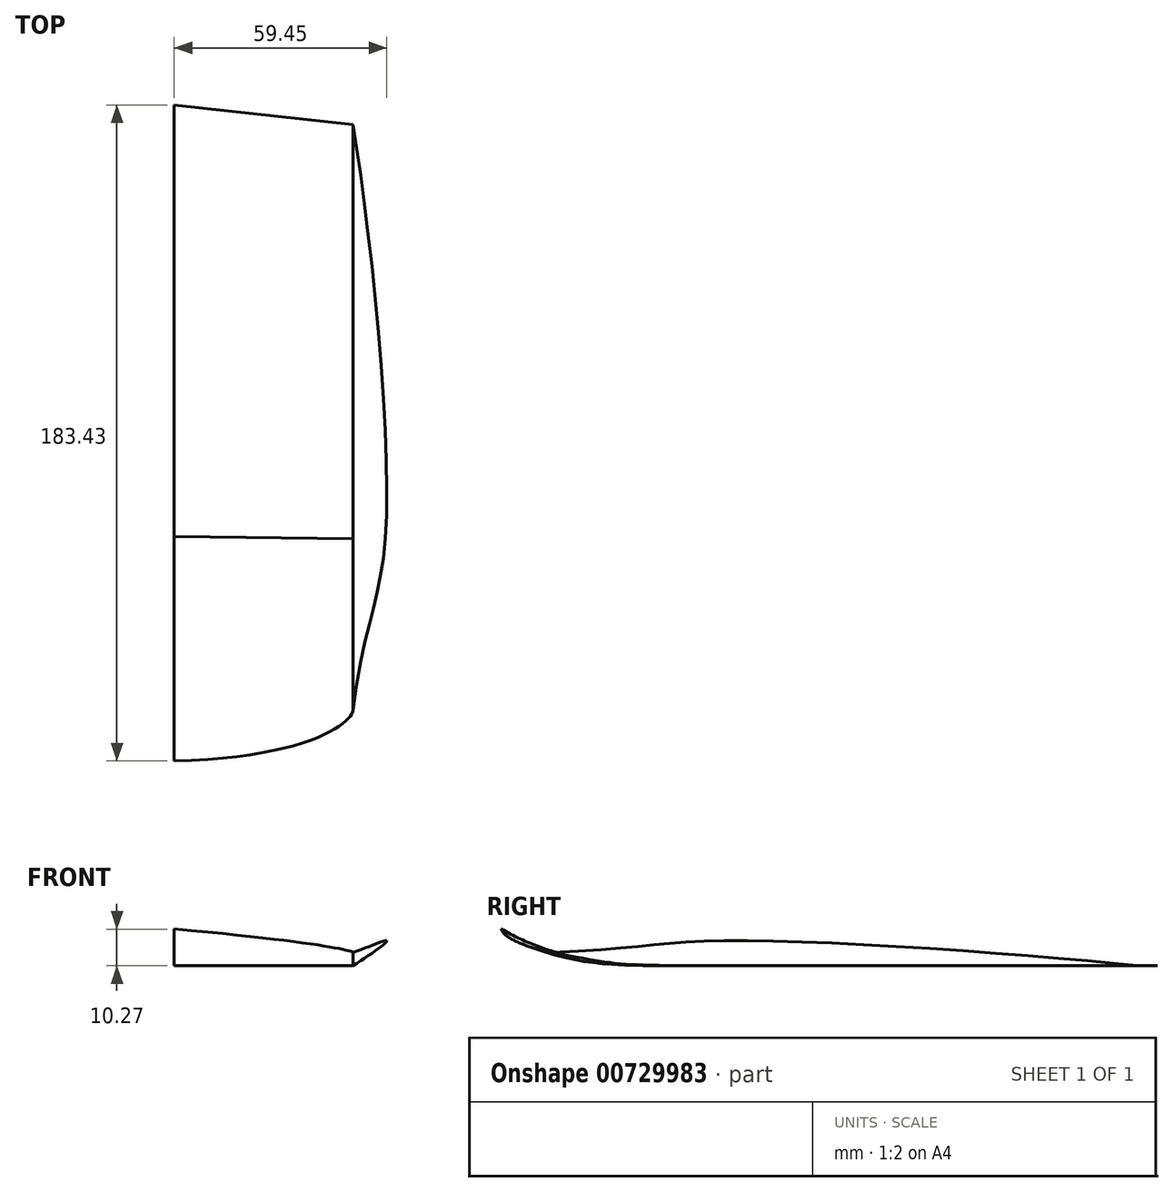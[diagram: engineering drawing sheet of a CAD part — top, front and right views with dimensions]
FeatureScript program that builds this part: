
annotation { "Feature Type Name" : "Feature", "Feature Type Description" : "" }
export const myFeature = defineFeature(function(context is Context, id is Id, definition is map)
    precondition{}
    {
        {
            var Q0;
            Q0=qCreatedBy(makeId("Right.planeOp"),FACE);
            var sketch = newSketch(context, id + "F0", { "sketchPlane" : qUnion([Q0])});
            skLineSegment(sketch, "E0", {"start": v(0, 0) * mm, "end": v(-120.64, 0) * mm});
            skFitSpline(sketch, "E1", {"points": [v(-120.64, 0) * mm, v(-183.43, 10.21) * mm], "startDerivative": vector(-83.56, 0) * mm, "endDerivative": vector(-53.29, 30.64) * mm});
            skSolve(sketch);
        }
        {
            var Q0;
            Q0=qCreatedBy(makeId("Right.planeOp"),FACE);
            cPlane(context, id + "F1", {"entities" : qUnion([Q0]), "cplaneType" : CPlaneType.OFFSET, "offset" : 50 * mm, "width" : 150 * mm, "height" : 150 * mm});
        }
        {
            var Q0;
            Q0=qCreatedBy(id+"F1.planeOp",FACE);
            var sketch = newSketch(context, id + "F2", { "sketchPlane" : qUnion([Q0])});
            skLineSegment(sketch, "E2", {"start": v(-5.5, 0) * mm, "end": v(-121.26, 0) * mm});
            skFitSpline(sketch, "E3", {"points": [v(-121.26, 0) * mm, v(-169.22, 3.7) * mm], "startDerivative": vector(-90.6, 0) * mm, "endDerivative": vector(-57, 11.1) * mm});
            skSolve(sketch);
        }
        {
            var Q0;
            Q0=sQuery(id+"F2.wireOp",VERTEX,"E3.end");
            var Q1;
            Q1=sQuery(id+"F0.wireOp",VERTEX,"E1.end");
            var Q2;
            Q2=sQuery(id+"F0.wireOp",VERTEX,"E0.end");
            cPlane(context, id + "F3", {"entities" : qUnion([Q0, Q1, Q2]), "cplaneType" : CPlaneType.THREE_POINT, "offset" : 0 * mm, "width" : 150 * mm, "height" : 150 * mm});
        }
        {
            var Q0;
            Q0=qCreatedBy(id+"F3.planeOp",FACE);
            var sketch = newSketch(context, id + "F4", { "sketchPlane" : qUnion([Q0])});
            skPoint(sketch, "E4", {"position": v(1.6, -182.69) * mm});
            skPoint(sketch, "E5", {"position": v(51.77, -167.62) * mm});
            skFitSpline(sketch, "E6", {"points": [v(1.6, -182.69) * mm, v(51.77, -167.62) * mm], "startDerivative": vector(114.51, 4.66) * mm, "endDerivative": vector(1.48, 10.64) * mm});
            skSolve(sketch);
        }
        {
            var Q0;
            Q0=sQuery(id+"F0.wireOp",EDGE,"E1");
            var Q1;
            Q1=sQuery(id+"F2.wireOp",EDGE,"E3");
            var Q2;
            Q2=sQuery(id+"F4.wireOp",EDGE,"E6");
            loft(context, id + "F5", {"bodyType" : ToolBodyType.SURFACE, "addGuides" : true, "wireProfilesArray" : [{ "wireProfileEntities" : qUnion([Q0]) }, { "wireProfileEntities" : qUnion([Q1]) }], "guidesArray" : [{ "guideEntities" : qUnion([Q2]), "guideDerivativeType" : LoftGuideDerivativeType.DEFAULT, "guideDerivativeMagnitude" : 1 }]});
        }
        {
            var Q0;
            Q0=sQuery(id+"F2.wireOp",EDGE,"E2");
            var Q1;
            Q1=sQuery(id+"F0.wireOp",EDGE,"E0");
            loft(context, id + "F6", {"bodyType" : ToolBodyType.SURFACE, "wireProfilesArray" : [{ "wireProfileEntities" : qUnion([Q0]) }, { "wireProfileEntities" : qUnion([Q1]) }]});
        }
        {
            var Q0;
            Q0=qCreatedBy(makeId("Top.planeOp"),FACE);
            cPlane(context, id + "F7", {"entities" : qUnion([Q0]), "cplaneType" : CPlaneType.OFFSET, "offset" : 7 * mm, "width" : 150 * mm, "height" : 150 * mm});
        }
        {
            var Q0;
            Q0=qCreatedBy(id+"F7.planeOp",FACE);
            var sketch = newSketch(context, id + "F8", { "sketchPlane" : qUnion([Q0])});
            skPoint(sketch, "E7", {"position": v(59.08, -120.45) * mm});
            skSolve(sketch);
        }
        {
            var Q0;
            Q0=sQuery(id+"F8.wireOp",VERTEX,"E7");
            var Q1;
            Q1=sQuery(id+"F4.wireOp",VERTEX,"E5");
            var Q2;
            Q2=sQuery(id+"F2.wireOp",VERTEX,"E2.start");
            cPlane(context, id + "F9", {"entities" : qUnion([Q0, Q1, Q2]), "cplaneType" : CPlaneType.THREE_POINT, "offset" : 25 * mm, "width" : 150 * mm, "height" : 150 * mm});
        }
        {
            var Q0;
            Q0=qCreatedBy(id+"F9.planeOp",FACE);
            var sketch = newSketch(context, id + "F10", { "sketchPlane" : qUnion([Q0])});
            skPoint(sketch, "E8", {"position": v(44.94, -169.26) * mm});
            skPoint(sketch, "E9", {"position": v(55.03, -120.58) * mm});
            skPoint(sketch, "E10", {"position": v(44.94, -5.5) * mm});
            skFitSpline(sketch, "E11", {"points": [v(44.94, -169.26) * mm, v(55.03, -120.58) * mm, v(44.94, -5.5) * mm], "startDerivative": vector(24.88, 183.26) * mm, "endDerivative": vector(-26.24, 143.19) * mm});
            skSolve(sketch);
        }
        {
            var Q0;
            Q0=sQuery(id+"F10.wireOp",EDGE,"E11");
            var Q1;
            Q1=sQuery(id+"F2.wireOp",EDGE,"E3");
            loft(context, id + "F11", {"bodyType" : ToolBodyType.SURFACE, "surfaceOperationType" : NewSurfaceOperationType.ADD, "wireProfilesArray" : [{ "wireProfileEntities" : qUnion([Q0]) }, { "wireProfileEntities" : qUnion([Q1]) }]});
        }
    });
